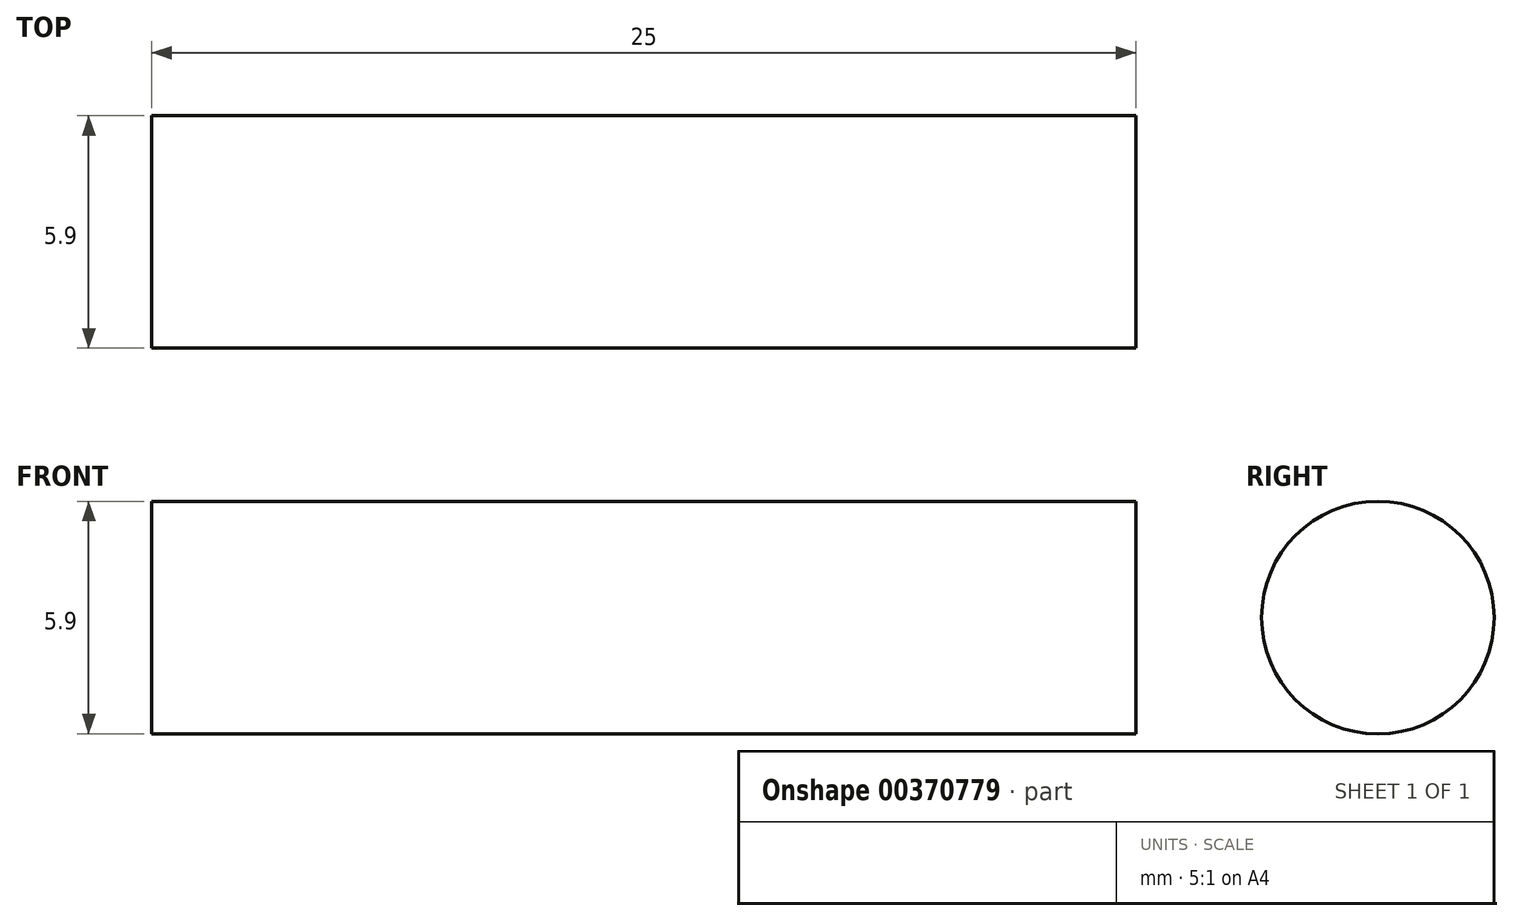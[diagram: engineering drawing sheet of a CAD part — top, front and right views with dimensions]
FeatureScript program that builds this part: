
annotation { "Feature Type Name" : "Feature", "Feature Type Description" : "" }
export const myFeature = defineFeature(function(context is Context, id is Id, definition is map)
    precondition{}
    {
        {
            var Q0;
            Q0=qCreatedBy(makeId("Front.planeOp"),FACE);
            var sketch = newSketch(context, id + "F0", { "sketchPlane" : qUnion([Q0])});
            skLineSegment(sketch, "E0", {"start": v(-27.82, 0) * mm, "end": v(29.32, 0) * mm, "construction": true});
            skLineSegment(sketch, "E1.bottom", {"start": v(-12.5, 0) * mm, "end": v(12.5, 0) * mm});
            skLineSegment(sketch, "E1.top", {"start": v(-12.5, 2.95) * mm, "end": v(12.5, 2.95) * mm});
            skLineSegment(sketch, "E1.left", {"start": v(-12.5, 0) * mm, "end": v(-12.5, 2.95) * mm});
            skLineSegment(sketch, "E1.right", {"start": v(12.5, 0) * mm, "end": v(12.5, 2.95) * mm});
            skSolve(sketch);
        }
        {
            var Q0;
            Q0=makeQuery(id+"F0.imprint","IMPRINT",FACE,{"disambiguationData":[TD([[makeQuery(id+"F0.imprint","IMPRINT",EDGE,{"derivedFrom":sQuery(id+"F0.wireOp",EDGE,"E1.bottom")}),1.0]])]});
            var Q1;
            Q1=sQuery(id+"F0.wireOp",EDGE,"E0");
            revolve(context, id + "F1", {"entities" : qUnion([Q0]), "axis" : qUnion([Q1]), "revolveType" : RevolveType.ONE_DIRECTION, "oppositeDirection" : true, "angle" : 360 * degree});
        }
    });
